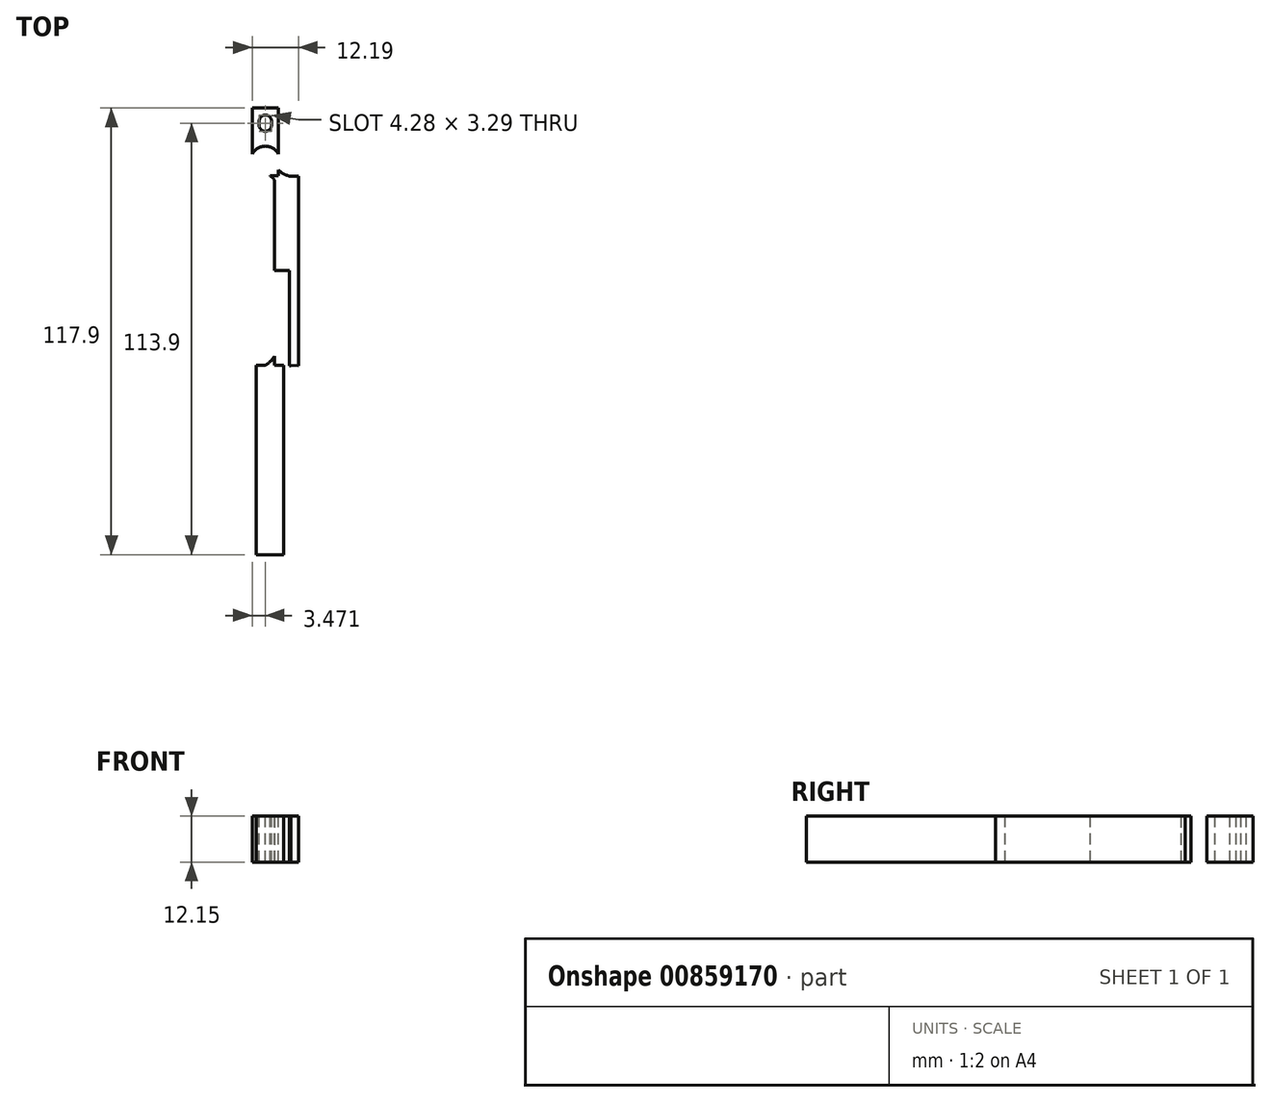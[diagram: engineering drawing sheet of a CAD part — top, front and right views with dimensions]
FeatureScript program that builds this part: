
annotation { "Feature Type Name" : "Feature", "Feature Type Description" : "" }
export const myFeature = defineFeature(function(context is Context, id is Id, definition is map)
    precondition{}
    {
        {
            var Q0;
            Q0=qCreatedBy(makeId("Top.planeOp"),FACE);
            var sketch = newSketch(context, id + "F0", { "sketchPlane" : qUnion([Q0])});
            skLineSegment(sketch, "E0.bottom", {"start": v(0, 0) * mm, "end": v(6.95, 0) * mm});
            skLineSegment(sketch, "E0.top", {"start": v(0, 17.9) * mm, "end": v(6.95, 17.9) * mm});
            skLineSegment(sketch, "E0.left", {"start": v(0, 0) * mm, "end": v(0, 17.9) * mm});
            skLineSegment(sketch, "E0.right", {"start": v(6.95, 0) * mm, "end": v(6.95, 17.9) * mm});
            skLineSegment(sketch, "E1", {"start": v(0, 0) * mm, "end": v(0, 7.85) * mm});
            skLineSegment(sketch, "E2", {"start": v(3.48, 0) * mm, "end": v(3.48, 7.85) * mm});
            skLineSegment(sketch, "E3", {"start": v(3.48, 7.85) * mm, "end": v(3.48, 6.9) * mm});
            skCircle(sketch, "E4", {"center": v(3.48, 3.92) * mm, "radius": 3.92 * mm});
            skLineSegment(sketch, "E5", {"start": v(3.47, 17.9) * mm, "end": v(3.47, 16.05) * mm});
            skLineSegment(sketch, "E6", {"start": v(3.47, 16.05) * mm, "end": v(3.48, 11.75) * mm});
            skLineSegment(sketch, "E7", {"start": v(3.47, 13.9) * mm, "end": v(3.47, 16.05) * mm});
            skLineSegment(sketch, "E8", {"start": v(3.48, 11.75) * mm, "end": v(3.47, 13.9) * mm});
            skLineSegment(sketch, "E9", {"start": v(4.55, 12.83) * mm, "end": v(4.55, 14.98) * mm});
            skLineSegment(sketch, "E10.bottom", {"start": v(3.48, 0) * mm, "end": v(1.03, 0) * mm});
            skLineSegment(sketch, "E10.top", {"start": v(3.48, -100) * mm, "end": v(1.03, -100) * mm});
            skLineSegment(sketch, "E10.left", {"start": v(3.48, 0) * mm, "end": v(3.48, -100) * mm});
            skLineSegment(sketch, "E10.right", {"start": v(1.03, 0) * mm, "end": v(1.03, -100) * mm});
            skLineSegment(sketch, "E11.bottom", {"start": v(3.48, 0) * mm, "end": v(5.93, 0) * mm});
            skLineSegment(sketch, "E11.top", {"start": v(3.48, -100) * mm, "end": v(5.93, -100) * mm});
            skLineSegment(sketch, "E11.right", {"start": v(5.93, 0) * mm, "end": v(5.93, -100) * mm});
            skLineSegment(sketch, "E12", {"start": v(5.93, 0) * mm, "end": v(5.93, 1.16) * mm});
            skLineSegment(sketch, "E13", {"start": v(1.03, 0) * mm, "end": v(1.02, 1.22) * mm});
            skLineSegment(sketch, "E14.bottom", {"start": v(6.95, 0) * mm, "end": v(9.83, -0.08) * mm});
            skLineSegment(sketch, "E14.left", {"start": v(6.95, 0) * mm, "end": v(6.95, 1.5) * mm});
            skLineSegment(sketch, "E15.right", {"start": v(5.93, -0.08) * mm, "end": v(5.93, -100) * mm});
            skLineSegment(sketch, "E16", {"start": v(3.48, 0) * mm, "end": v(3.48, -12.11) * mm});
            skLineSegment(sketch, "E17", {"start": v(3.48, 0) * mm, "end": v(3.48, -25) * mm});
            skLineSegment(sketch, "E18", {"start": v(3.48, -25) * mm, "end": v(1.03, -25) * mm});
            skLineSegment(sketch, "E19", {"start": v(1.03, -25) * mm, "end": v(1.03, -25.71) * mm});
            skLineSegment(sketch, "E20", {"start": v(1.03, -25) * mm, "end": v(1.03, -30) * mm});
            skLineSegment(sketch, "E21", {"start": v(5.93, -25) * mm, "end": v(5.93, -50) * mm});
            skPoint(sketch, "E21.startSnap0", {"position": v(2.25, -25) * mm});
            skLineSegment(sketch, "E22", {"start": v(5.93, -50) * mm, "end": v(9.83, -50.04) * mm});
            skLineSegment(sketch, "E23", {"start": v(3.48, -50) * mm, "end": v(1.03, -50) * mm});
            skLineSegment(sketch, "E24", {"start": v(5.93, -25) * mm, "end": v(9.83, -25) * mm});
            skLineSegment(sketch, "E25", {"start": v(5.93, -25) * mm, "end": v(5.93, -21.38) * mm});
            skLineSegment(sketch, "E26", {"start": v(5.93, -25) * mm, "end": v(5.93, -22.99) * mm});
            skLineSegment(sketch, "E27", {"start": v(3.48, -25) * mm, "end": v(3.48, -26.23) * mm});
            skLineSegment(sketch, "E28", {"start": v(5.93, -50) * mm, "end": v(5.93, -52.01) * mm});
            skLineSegment(sketch, "E29", {"start": v(3.48, -50) * mm, "end": v(3.48, -48.78) * mm});
            skLineSegment(sketch, "E30", {"start": v(5.93, -25) * mm, "end": v(5.93, -26.95) * mm});
            skLineSegment(sketch, "E31", {"start": v(3.48, -50) * mm, "end": v(5.93, -50) * mm});
            skLineSegment(sketch, "E32", {"start": v(3.48, 0) * mm, "end": v(3.48, -1.23) * mm});
            skLineSegment(sketch, "E33", {"start": v(6.95, 0) * mm, "end": v(6.95, 1.44) * mm});
            skFitSpline(sketch, "E34", {"points": [v(6.95, 1.5) * mm, v(9.83, -0.08) * mm], "startDerivative": vector(2.42, -2.4) * mm, "endDerivative": vector(3.34, -1.08) * mm});
            skLineSegment(sketch, "E35", {"start": v(1.03, 0) * mm, "end": v(1.03, -0.69) * mm});
            skLineSegment(sketch, "E36", {"start": v(1.03, 0) * mm, "end": v(1.03, -1) * mm});
            skLineSegment(sketch, "E37", {"start": v(5.92, 0) * mm, "end": v(5.93, -1.23) * mm});
            skFitSpline(sketch, "E38", {"points": [v(4.7, 0) * mm, v(5.93, -1.23) * mm], "startDerivative": vector(1.66, -0.95) * mm, "endDerivative": vector(0.86, -1.52) * mm});
            skLineSegment(sketch, "E39", {"start": v(5.93, -25) * mm, "end": v(5.93, -28.9) * mm});
            skLineSegment(sketch, "E40", {"start": v(3.48, -25) * mm, "end": v(5.93, -25) * mm});
            skLineSegment(sketch, "E41", {"start": v(5.93, -25) * mm, "end": v(5.93, -22.55) * mm});
            skLineSegment(sketch, "E42", {"start": v(5.93, -50) * mm, "end": v(5.93, -47.55) * mm});
            skFitSpline(sketch, "E43", {"points": [v(5.93, -47.55) * mm, v(3.48, -50) * mm], "startDerivative": vector(-2.07, -3.53) * mm, "endDerivative": vector(-2.94, -2.05) * mm});
            skLineSegment(sketch, "E44.left", {"start": v(5.93, -50) * mm, "end": v(5.93, -100) * mm});
            skLineSegment(sketch, "E45", {"start": v(9.83, -0.08) * mm, "end": v(9.83, -50.04) * mm});
            skLineSegment(sketch, "E46.bottom", {"start": v(9.83, -0.08) * mm, "end": v(12.2, -0.08) * mm});
            skLineSegment(sketch, "E46.top", {"start": v(9.83, -50.08) * mm, "end": v(12.2, -50.08) * mm});
            skLineSegment(sketch, "E46.left", {"start": v(9.83, -0.08) * mm, "end": v(9.83, -50.08) * mm});
            skLineSegment(sketch, "E46.right", {"start": v(12.2, -0.08) * mm, "end": v(12.2, -50.08) * mm});
            skLineSegment(sketch, "E47.bottom", {"start": v(5.93, -50) * mm, "end": v(8.3, -50) * mm});
            skLineSegment(sketch, "E47.top", {"start": v(5.93, -100) * mm, "end": v(8.3, -100) * mm});
            skLineSegment(sketch, "E47.right", {"start": v(8.3, -50) * mm, "end": v(8.3, -100) * mm});
            skLineSegment(sketch, "E48", {"start": v(8.3, -50) * mm, "end": v(12.2, -50.08) * mm});
            skLineSegment(sketch, "E49", {"start": v(8.3, -50) * mm, "end": v(8.3, -53.9) * mm});
            skFitSpline(sketch, "E50", {"points": [v(8.3, -53.9) * mm, v(10.24, -50.04) * mm], "startDerivative": vector(0.85, 4.55) * mm, "endDerivative": vector(3.1, 3.55) * mm});
            skCircle(sketch, "E51", {"center": v(3.48, 3.92) * mm, "radius": 3.28 * mm});
            skLineSegment(sketch, "E52", {"start": v(3.47, 13.9) * mm, "end": v(3.47, 12.9) * mm});
            skLineSegment(sketch, "E53", {"start": v(3.47, 13.9) * mm, "end": v(3.47, 14.9) * mm});
            skCircle(sketch, "E54", {"center": v(3.47, 13.4) * mm, "radius": 1.64 * mm});
            skArc(sketch, "E55", {"start": v(5.1, 14.7) * mm, "mid": v(1.83, 14.37) * mm, "end": v(5.1, 14.14) * mm});
            skLineSegment(sketch, "E56", {"start": v(3.48, 11.75) * mm, "end": v(1.27, 11.75) * mm});
            skLineSegment(sketch, "E57", {"start": v(3.48, 11.75) * mm, "end": v(5.93, 11.75) * mm});
            skLineSegment(sketch, "E58", {"start": v(3.47, 16.05) * mm, "end": v(1.21, 16.05) * mm});
            skLineSegment(sketch, "E59", {"start": v(3.47, 16.05) * mm, "end": v(5.69, 16.05) * mm});
            skLineSegment(sketch, "E60", {"start": v(5.11, 13.43) * mm, "end": v(5.1, 14.7) * mm});
            skLineSegment(sketch, "E61", {"start": v(1.84, 13.46) * mm, "end": v(1.83, 14.38) * mm});
            skSolve(sketch);
        }
        {
            var Q0;
            Q0=makeQuery(id+"F0.imprint","IMPRINT",FACE,{"disambiguationData":[TD([[makeQuery(id+"F0.imprint","IMPRINT",EDGE,{"derivedFrom":sQuery(id+"F0.wireOp",EDGE,"E14.bottom")}),1.0]])]});
            var Q1;
            {var subQ0=sQuery(id+"F0.wireOp",EDGE,"E4");var subQ3=sQuery(id+"F0.wireOp",EDGE,"E0.right");var subQ10=makeQuery(id+"F0.imprint","INTERSECT",VERTEX,{"disambiguationData":[OD(0.0)],"derivedFrom":[subQ3,subQ0]});Q1=makeQuery(id+"F0.imprint","IMPRINT",FACE,{"disambiguationData":[TD([[makeQuery(id+"F0.imprint","IMPRINT",EDGE,{"disambiguationData":[TD([[subQ10,-1.0]])],"derivedFrom":subQ3}),1.0]])]});}
            var Q2;
            {var subQ0=sQuery(id+"F0.wireOp",EDGE,"E4");var subQ1=sQuery(id+"F0.wireOp",EDGE,"E0.right");var subQ2=makeQuery(id+"F0.imprint","INTERSECT",VERTEX,{"disambiguationData":[OD(0.0)],"derivedFrom":[subQ1,subQ0]});Q2=makeQuery(id+"F0.imprint","IMPRINT",FACE,{"disambiguationData":[TD([[makeQuery(id+"F0.imprint","IMPRINT",EDGE,{"disambiguationData":[TD([[subQ2,-1.0]])],"derivedFrom":subQ1}),-1.0]])]});}
            var Q3;
            {var subQ0=sQuery(id+"F0.wireOp",EDGE,"E14.left");Q3=makeQuery(id+"F0.imprint","IMPRINT",FACE,{"disambiguationData":[TD([[makeQuery(id+"F0.imprint","IMPRINT",EDGE,{"derivedFrom":subQ0}),1.0]])]});}
            var Q4;
            {var subQ0=sQuery(id+"F0.wireOp",EDGE,"E11.bottom");var subQ5=makeQuery(id+"F0.imprint","INTERSECT",VERTEX,{"derivedFrom":[subQ0,sQuery(id+"F0.wireOp",EDGE,"E38")]});Q4=makeQuery(id+"F0.imprint","IMPRINT",FACE,{"disambiguationData":[TD([[makeQuery(id+"F0.imprint","IMPRINT",EDGE,{"disambiguationData":[TD([[subQ5,-1.0]])],"derivedFrom":subQ0}),1.0]])]});}
            var Q5;
            {var subQ0=sQuery(id+"F0.wireOp",EDGE,"E4");var subQ5=sQuery(id+"F0.wireOp",EDGE,"E1");var subQ10=makeQuery(id+"F0.imprint","INTERSECT",VERTEX,{"disambiguationData":[OD(0.0)],"derivedFrom":[subQ5,subQ0]});Q5=makeQuery(id+"F0.imprint","IMPRINT",FACE,{"disambiguationData":[TD([[makeQuery(id+"F0.imprint","IMPRINT",EDGE,{"disambiguationData":[TD([[subQ10,-1.0]])],"derivedFrom":subQ5}),-1.0]])]});}
            var Q6;
            {var subQ0=sQuery(id+"F0.wireOp",EDGE,"E10.bottom");Q6=makeQuery(id+"F0.imprint","IMPRINT",FACE,{"disambiguationData":[TD([[makeQuery(id+"F0.imprint","IMPRINT",EDGE,{"derivedFrom":subQ0}),-1.0]])]});}
            var Q7;
            {var subQ0=sQuery(id+"F0.wireOp",EDGE,"E1");var subQ1=sQuery(id+"F0.wireOp",EDGE,"E0.bottom");var subQ2=makeQuery(id+"F0.imprint","INTERSECT",VERTEX,{"derivedFrom":[subQ1,subQ0]});Q7=makeQuery(id+"F0.imprint","IMPRINT",FACE,{"disambiguationData":[TD([[makeQuery(id+"F0.imprint","IMPRINT",EDGE,{"disambiguationData":[TD([[subQ2,-1.0]])],"derivedFrom":subQ0}),-1.0]])]});}
            var Q8;
            {var subQ0=sQuery(id+"F0.wireOp",EDGE,"E4");var subQ1=sQuery(id+"F0.wireOp",EDGE,"E1");var subQ2=makeQuery(id+"F0.imprint","INTERSECT",VERTEX,{"disambiguationData":[OD(0.0)],"derivedFrom":[subQ1,subQ0]});Q8=makeQuery(id+"F0.imprint","IMPRINT",FACE,{"disambiguationData":[TD([[makeQuery(id+"F0.imprint","IMPRINT",EDGE,{"disambiguationData":[TD([[subQ2,-1.0]])],"derivedFrom":subQ1}),1.0]])]});}
            var Q9;
            {var subQ4=sQuery(id+"F0.wireOp",EDGE,"E0.left");Q9=makeQuery(id+"F0.imprint","IMPRINT",FACE,{"disambiguationData":[TD([[makeQuery(id+"F0.imprint","IMPRINT",EDGE,{"derivedFrom":subQ4}),-1.0]])]});}
            var Q10;
            {var subQ4=sQuery(id+"F0.wireOp",EDGE,"E14.bottom");Q10=makeQuery(id+"F0.imprint","IMPRINT",FACE,{"disambiguationData":[TD([[makeQuery(id+"F0.imprint","IMPRINT",EDGE,{"derivedFrom":subQ4}),-1.0]])]});}
            var Q11;
            {var subQ3=sQuery(id+"F0.wireOp",EDGE,"E38");Q11=makeQuery(id+"F0.imprint","IMPRINT",FACE,{"disambiguationData":[TD([[makeQuery(id+"F0.imprint","IMPRINT",EDGE,{"derivedFrom":subQ3}),1.0]])]});}
            var Q12;
            {var subQ3=sQuery(id+"F0.wireOp",EDGE,"E21");Q12=makeQuery(id+"F0.imprint","IMPRINT",FACE,{"disambiguationData":[TD([[makeQuery(id+"F0.imprint","IMPRINT",EDGE,{"derivedFrom":subQ3}),1.0]])]});}
            var Q13;
            {var subQ0=sQuery(id+"F0.wireOp",EDGE,"E28");Q13=makeQuery(id+"F0.imprint","IMPRINT",FACE,{"disambiguationData":[TD([[makeQuery(id+"F0.imprint","IMPRINT",EDGE,{"derivedFrom":subQ0}),1.0]])]});}
            var Q14;
            Q14=makeQuery(id+"F0.imprint","IMPRINT",FACE,{"disambiguationData":[TD([[makeQuery(id+"F0.imprint","IMPRINT",EDGE,{"derivedFrom":sQuery(id+"F0.wireOp",EDGE,"E31")}),1.0]])]});
            var Q15;
            {var subQ2=sQuery(id+"F0.wireOp",EDGE,"E11.top");Q15=makeQuery(id+"F0.imprint","IMPRINT",FACE,{"disambiguationData":[TD([[makeQuery(id+"F0.imprint","IMPRINT",EDGE,{"derivedFrom":subQ2}),1.0]])]});}
            var Q16;
            {var subQ0=sQuery(id+"F0.wireOp",EDGE,"E10.top");Q16=makeQuery(id+"F0.imprint","IMPRINT",FACE,{"disambiguationData":[TD([[makeQuery(id+"F0.imprint","IMPRINT",EDGE,{"derivedFrom":subQ0}),-1.0]])]});}
            extrude(context, id + "F1", {"entities" : qUnion([Q0, Q1, Q2, Q3, Q4, Q5, Q6, Q7, Q8, Q9, Q10, Q11, Q12, Q13, Q14, Q15, Q16]), "depth" : -2.5 * mm, "offsetDistance" : 25 * mm});
        }
        {
            var Q0;
            {var subQ0=sQuery(id+"F0.wireOp",EDGE,"E4");var subQ3=sQuery(id+"F0.wireOp",EDGE,"E0.right");var subQ10=makeQuery(id+"F0.imprint","INTERSECT",VERTEX,{"disambiguationData":[OD(0.0)],"derivedFrom":[subQ3,subQ0]});Q0=makeQuery(id+"F0.imprint","IMPRINT",FACE,{"disambiguationData":[TD([[makeQuery(id+"F0.imprint","IMPRINT",EDGE,{"disambiguationData":[TD([[subQ10,-1.0]])],"derivedFrom":subQ3}),1.0]])]});}
            var Q1;
            {var subQ0=sQuery(id+"F0.wireOp",EDGE,"E4");var subQ5=sQuery(id+"F0.wireOp",EDGE,"E1");var subQ10=makeQuery(id+"F0.imprint","INTERSECT",VERTEX,{"disambiguationData":[OD(0.0)],"derivedFrom":[subQ5,subQ0]});Q1=makeQuery(id+"F0.imprint","IMPRINT",FACE,{"disambiguationData":[TD([[makeQuery(id+"F0.imprint","IMPRINT",EDGE,{"disambiguationData":[TD([[subQ10,-1.0]])],"derivedFrom":subQ5}),-1.0]])]});}
            var Q2;
            {var subQ0=sQuery(id+"F0.wireOp",EDGE,"E4");var subQ1=sQuery(id+"F0.wireOp",EDGE,"E0.right");var subQ2=makeQuery(id+"F0.imprint","INTERSECT",VERTEX,{"disambiguationData":[OD(0.0)],"derivedFrom":[subQ1,subQ0]});Q2=makeQuery(id+"F0.imprint","IMPRINT",FACE,{"disambiguationData":[TD([[makeQuery(id+"F0.imprint","IMPRINT",EDGE,{"disambiguationData":[TD([[subQ2,-1.0]])],"derivedFrom":subQ1}),-1.0]])]});}
            var Q3;
            {var subQ0=sQuery(id+"F0.wireOp",EDGE,"E4");var subQ1=sQuery(id+"F0.wireOp",EDGE,"E1");var subQ2=makeQuery(id+"F0.imprint","INTERSECT",VERTEX,{"disambiguationData":[OD(0.0)],"derivedFrom":[subQ1,subQ0]});Q3=makeQuery(id+"F0.imprint","IMPRINT",FACE,{"disambiguationData":[TD([[makeQuery(id+"F0.imprint","IMPRINT",EDGE,{"disambiguationData":[TD([[subQ2,-1.0]])],"derivedFrom":subQ1}),1.0]])]});}
            var Q4;
            Q4=makeQuery(id+"F0.imprint","IMPRINT",FACE,{"disambiguationData":[TD([[makeQuery(id+"F0.imprint","IMPRINT",EDGE,{"derivedFrom":sQuery(id+"F0.wireOp",EDGE,"E14.bottom")}),1.0]])]});
            var Q5;
            {var subQ0=sQuery(id+"F0.wireOp",EDGE,"E14.left");Q5=makeQuery(id+"F0.imprint","IMPRINT",FACE,{"disambiguationData":[TD([[makeQuery(id+"F0.imprint","IMPRINT",EDGE,{"derivedFrom":subQ0}),1.0]])]});}
            var Q6;
            {var subQ0=sQuery(id+"F0.wireOp",EDGE,"E11.bottom");var subQ5=makeQuery(id+"F0.imprint","INTERSECT",VERTEX,{"derivedFrom":[subQ0,sQuery(id+"F0.wireOp",EDGE,"E38")]});Q6=makeQuery(id+"F0.imprint","IMPRINT",FACE,{"disambiguationData":[TD([[makeQuery(id+"F0.imprint","IMPRINT",EDGE,{"disambiguationData":[TD([[subQ5,-1.0]])],"derivedFrom":subQ0}),1.0]])]});}
            var Q7;
            {var subQ0=sQuery(id+"F0.wireOp",EDGE,"E10.bottom");Q7=makeQuery(id+"F0.imprint","IMPRINT",FACE,{"disambiguationData":[TD([[makeQuery(id+"F0.imprint","IMPRINT",EDGE,{"derivedFrom":subQ0}),-1.0]])]});}
            var Q8;
            {var subQ0=sQuery(id+"F0.wireOp",EDGE,"E1");var subQ1=sQuery(id+"F0.wireOp",EDGE,"E0.bottom");var subQ2=makeQuery(id+"F0.imprint","INTERSECT",VERTEX,{"derivedFrom":[subQ1,subQ0]});Q8=makeQuery(id+"F0.imprint","IMPRINT",FACE,{"disambiguationData":[TD([[makeQuery(id+"F0.imprint","IMPRINT",EDGE,{"disambiguationData":[TD([[subQ2,-1.0]])],"derivedFrom":subQ0}),-1.0]])]});}
            var Q9;
            {var subQ4=sQuery(id+"F0.wireOp",EDGE,"E14.bottom");Q9=makeQuery(id+"F0.imprint","IMPRINT",FACE,{"disambiguationData":[TD([[makeQuery(id+"F0.imprint","IMPRINT",EDGE,{"derivedFrom":subQ4}),-1.0]])]});}
            var Q10;
            {var subQ3=sQuery(id+"F0.wireOp",EDGE,"E38");Q10=makeQuery(id+"F0.imprint","IMPRINT",FACE,{"disambiguationData":[TD([[makeQuery(id+"F0.imprint","IMPRINT",EDGE,{"derivedFrom":subQ3}),1.0]])]});}
            var Q11;
            {var subQ3=sQuery(id+"F0.wireOp",EDGE,"E21");Q11=makeQuery(id+"F0.imprint","IMPRINT",FACE,{"disambiguationData":[TD([[makeQuery(id+"F0.imprint","IMPRINT",EDGE,{"derivedFrom":subQ3}),1.0]])]});}
            var Q12;
            Q12=makeQuery(id+"F0.imprint","IMPRINT",FACE,{"disambiguationData":[TD([[makeQuery(id+"F0.imprint","IMPRINT",EDGE,{"derivedFrom":sQuery(id+"F0.wireOp",EDGE,"E31")}),1.0]])]});
            var Q13;
            {var subQ0=sQuery(id+"F0.wireOp",EDGE,"E28");Q13=makeQuery(id+"F0.imprint","IMPRINT",FACE,{"disambiguationData":[TD([[makeQuery(id+"F0.imprint","IMPRINT",EDGE,{"derivedFrom":subQ0}),1.0]])]});}
            var Q14;
            {var subQ2=sQuery(id+"F0.wireOp",EDGE,"E11.top");Q14=makeQuery(id+"F0.imprint","IMPRINT",FACE,{"disambiguationData":[TD([[makeQuery(id+"F0.imprint","IMPRINT",EDGE,{"derivedFrom":subQ2}),1.0]])]});}
            var Q15;
            {var subQ0=sQuery(id+"F0.wireOp",EDGE,"E10.top");Q15=makeQuery(id+"F0.imprint","IMPRINT",FACE,{"disambiguationData":[TD([[makeQuery(id+"F0.imprint","IMPRINT",EDGE,{"derivedFrom":subQ0}),-1.0]])]});}
            extrude(context, id + "F2", {"entities" : qUnion([Q0, Q1, Q2, Q3, Q4, Q5, Q6, Q7, Q8, Q9, Q10, Q11, Q12, Q13, Q14, Q15]), "operationType" : NewBodyOperationType.ADD, "depth" : 9.65 * mm, "offsetDistance" : 25 * mm});
        }
        {
            var Q0;
            {var subQ6=sQuery(id+"F0.wireOp",EDGE,"E46.bottom");Q0=makeQuery(id+"F0.imprint","IMPRINT",FACE,{"disambiguationData":[TD([[makeQuery(id+"F0.imprint","IMPRINT",EDGE,{"derivedFrom":subQ6}),-1.0]])]});}
            var Q1;
            {var subQ1=sQuery(id+"F0.wireOp",EDGE,"E47.top");Q1=makeQuery(id+"F0.imprint","IMPRINT",FACE,{"disambiguationData":[TD([[makeQuery(id+"F0.imprint","IMPRINT",EDGE,{"derivedFrom":subQ1}),1.0]])]});}
            var Q2;
            {var subQ3=sQuery(id+"F0.wireOp",EDGE,"E22");var subQ5=sQuery(id+"F0.wireOp",EDGE,"E46.left");var subQ6=makeQuery(id+"F0.imprint","INTERSECT",VERTEX,{"derivedFrom":[subQ3,subQ5]});Q2=makeQuery(id+"F0.imprint","IMPRINT",FACE,{"disambiguationData":[TD([[makeQuery(id+"F0.imprint","IMPRINT",EDGE,{"disambiguationData":[TD([[subQ6,1.0]])],"derivedFrom":subQ3}),-1.0]])]});}
            extrude(context, id + "F3", {"entities" : qUnion([Q0, Q1, Q2]), "operationType" : NewBodyOperationType.ADD, "depth" : -2.5 * mm, "offsetDistance" : 25 * mm});
        }
        {
            var Q0;
            {var subQ1=sQuery(id+"F0.wireOp",EDGE,"E47.top");Q0=makeQuery(id+"F0.imprint","IMPRINT",FACE,{"disambiguationData":[TD([[makeQuery(id+"F0.imprint","IMPRINT",EDGE,{"derivedFrom":subQ1}),1.0]])]});}
            var Q1;
            {var subQ3=sQuery(id+"F0.wireOp",EDGE,"E22");var subQ5=sQuery(id+"F0.wireOp",EDGE,"E46.left");var subQ6=makeQuery(id+"F0.imprint","INTERSECT",VERTEX,{"derivedFrom":[subQ3,subQ5]});Q1=makeQuery(id+"F0.imprint","IMPRINT",FACE,{"disambiguationData":[TD([[makeQuery(id+"F0.imprint","IMPRINT",EDGE,{"disambiguationData":[TD([[subQ6,1.0]])],"derivedFrom":subQ3}),-1.0]])]});}
            var Q2;
            {var subQ6=sQuery(id+"F0.wireOp",EDGE,"E46.bottom");Q2=makeQuery(id+"F0.imprint","IMPRINT",FACE,{"disambiguationData":[TD([[makeQuery(id+"F0.imprint","IMPRINT",EDGE,{"derivedFrom":subQ6}),-1.0]])]});}
            extrude(context, id + "F4", {"entities" : qUnion([Q0, Q1, Q2]), "operationType" : NewBodyOperationType.ADD, "depth" : 9.65 * mm, "offsetDistance" : 25 * mm});
        }
        {
            var Q0;
            {var subQ0=sQuery(id+"F0.wireOp",EDGE,"E46.left");var subQ1=sQuery(id+"F0.wireOp",EDGE,"E22");var subQ2=makeQuery(id+"F0.imprint","INTERSECT",VERTEX,{"derivedFrom":[subQ1,subQ0]});Q0=makeQuery(id+"F0.imprint","IMPRINT",FACE,{"disambiguationData":[TD([[makeQuery(id+"F0.imprint","IMPRINT",EDGE,{"disambiguationData":[TD([[subQ2,1.0]])],"derivedFrom":subQ1}),1.0]])]});}
            var Q1;
            {var subQ0=sQuery(id+"F0.wireOp",EDGE,"E47.bottom");Q1=makeQuery(id+"F0.imprint","IMPRINT",FACE,{"disambiguationData":[TD([[makeQuery(id+"F0.imprint","IMPRINT",EDGE,{"derivedFrom":subQ0}),-1.0]])]});}
            var Q2;
            {var subQ3=sQuery(id+"F0.wireOp",EDGE,"E46.left");var subQ6=sQuery(id+"F0.wireOp",EDGE,"E46.top");var subQ7=makeQuery(id+"F0.imprint","INTERSECT",VERTEX,{"derivedFrom":[subQ6,subQ3]});Q2=makeQuery(id+"F0.imprint","IMPRINT",FACE,{"disambiguationData":[TD([[makeQuery(id+"F0.imprint","IMPRINT",EDGE,{"disambiguationData":[TD([[subQ7,-1.0]])],"derivedFrom":subQ6}),1.0]])]});}
            extrude(context, id + "F5", {"entities" : qUnion([Q0, Q1, Q2]), "operationType" : NewBodyOperationType.ADD, "depth" : 9.65 * mm, "offsetDistance" : 25 * mm});
        }
        {
            var Q0;
            {var subQ3=sQuery(id+"F0.wireOp",EDGE,"E46.left");var subQ6=sQuery(id+"F0.wireOp",EDGE,"E46.top");var subQ7=makeQuery(id+"F0.imprint","INTERSECT",VERTEX,{"derivedFrom":[subQ6,subQ3]});Q0=makeQuery(id+"F0.imprint","IMPRINT",FACE,{"disambiguationData":[TD([[makeQuery(id+"F0.imprint","IMPRINT",EDGE,{"disambiguationData":[TD([[subQ7,-1.0]])],"derivedFrom":subQ6}),1.0]])]});}
            var Q1;
            {var subQ0=sQuery(id+"F0.wireOp",EDGE,"E46.left");var subQ1=sQuery(id+"F0.wireOp",EDGE,"E22");var subQ2=makeQuery(id+"F0.imprint","INTERSECT",VERTEX,{"derivedFrom":[subQ1,subQ0]});Q1=makeQuery(id+"F0.imprint","IMPRINT",FACE,{"disambiguationData":[TD([[makeQuery(id+"F0.imprint","IMPRINT",EDGE,{"disambiguationData":[TD([[subQ2,1.0]])],"derivedFrom":subQ1}),1.0]])]});}
            var Q2;
            {var subQ0=sQuery(id+"F0.wireOp",EDGE,"E47.bottom");Q2=makeQuery(id+"F0.imprint","IMPRINT",FACE,{"disambiguationData":[TD([[makeQuery(id+"F0.imprint","IMPRINT",EDGE,{"derivedFrom":subQ0}),-1.0]])]});}
            extrude(context, id + "F6", {"entities" : qUnion([Q0, Q1, Q2]), "operationType" : NewBodyOperationType.ADD, "depth" : -2.5 * mm, "offsetDistance" : 25 * mm});
        }
    });
